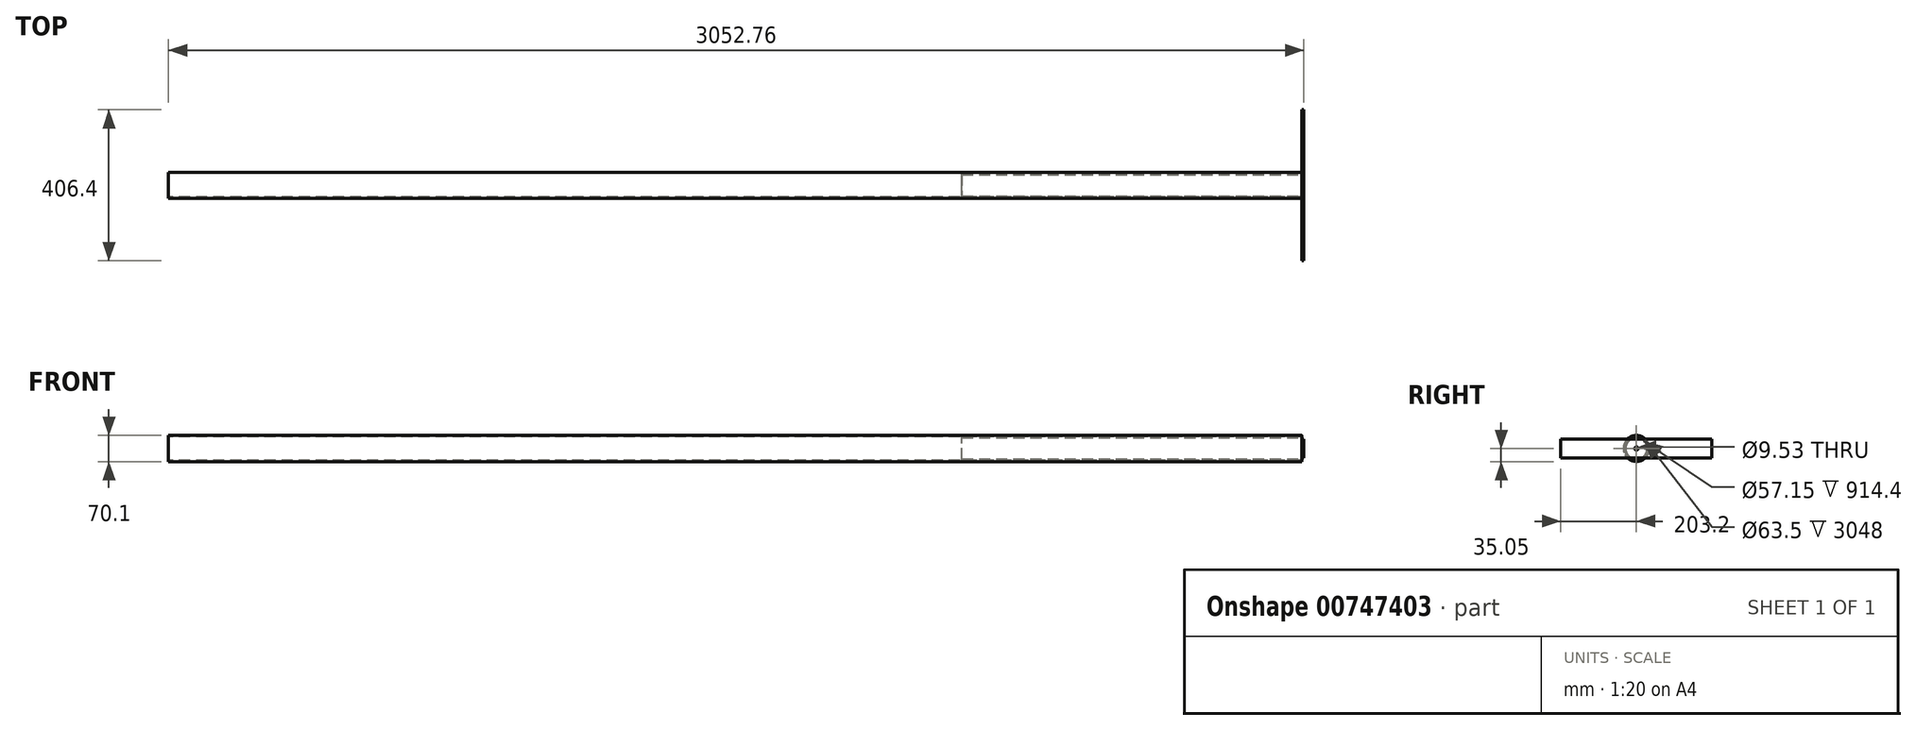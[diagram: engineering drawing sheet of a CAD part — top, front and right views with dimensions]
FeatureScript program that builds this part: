
annotation { "Feature Type Name" : "Feature", "Feature Type Description" : "" }
export const myFeature = defineFeature(function(context is Context, id is Id, definition is map)
    precondition{}
    {
        {
            var Q0;
            Q0=qCreatedBy(makeId("Right.planeOp"),FACE);
            var sketch = newSketch(context, id + "F0", { "sketchPlane" : qUnion([Q0])});
            skCircle(sketch, "E0", {"center": v(0, 0) * mm, "radius": 35.05 * mm});
            skCircle(sketch, "E1", {"center": v(0, 0) * mm, "radius": 31.75 * mm});
            skSolve(sketch);
        }
        {
            var Q0;
            Q0 = qSketchRegion(id + "F0", true);
            extrude(context, id + "F1", {"entities" : qUnion([Q0]), "endBound" : BoundingType.SYMMETRIC, "depth" : 3048 * mm, "offsetDistance" : 25.4 * mm});
        }
        {
            var Q0;
            Q0=makeQuery(id+"F1.opExtrude","CAP_FACE",FACE,{"disambiguationData":[OSD([sQuery(id+"F0.wireOp",EDGE,"E0"),sQuery(id+"F0.wireOp",EDGE,"E1")])],"isStart":false});
            var sketch = newSketch(context, id + "F2", { "sketchPlane" : qUnion([Q0])});
            skCircle(sketch, "E2", {"center": v(0, 0) * mm, "radius": 31.5 * mm});
            skCircle(sketch, "E3", {"center": v(0, 0) * mm, "radius": 28.58 * mm});
            skSolve(sketch);
        }
        {
            var Q0;
            Q0 = qSketchRegion(id + "F2", true);
            extrude(context, id + "F3", {"entities" : qUnion([Q0]), "oppositeDirection" : true, "depth" : 914.4 * mm, "offsetDistance" : 25.4 * mm});
        }
        {
            var Q0;
            Q0=makeQuery(id+"F1.opExtrude","CAP_FACE",FACE,{"disambiguationData":[OSD([sQuery(id+"F0.wireOp",EDGE,"E0"),sQuery(id+"F0.wireOp",EDGE,"E1")])],"isStart":false});
            var sketch = newSketch(context, id + "F4", { "sketchPlane" : qUnion([Q0])});
            skLineSegment(sketch, "E4.bottom", {"start": v(-203.2, -25.4) * mm, "end": v(203.2, -25.4) * mm});
            skLineSegment(sketch, "E4.top", {"start": v(-203.2, 25.4) * mm, "end": v(203.2, 25.4) * mm});
            skLineSegment(sketch, "E4.left", {"start": v(-203.2, -25.4) * mm, "end": v(-203.2, 25.4) * mm});
            skLineSegment(sketch, "E4.right", {"start": v(203.2, -25.4) * mm, "end": v(203.2, 25.4) * mm});
            skPoint(sketch, "E4.middle", {"position": v(0, 0) * mm});
            skSolve(sketch);
        }
        {
            var Q0;
            Q0 = qSketchRegion(id + "F4", true);
            extrude(context, id + "F5", {"entities" : qUnion([Q0]), "depth" : 4.76 * mm, "offsetDistance" : 25.4 * mm});
        }
        {
            var Q0;
            Q0=makeQuery(id+"F5.opExtrude","CAP_FACE",FACE,{"disambiguationData":[OSD([sQuery(id+"F4.wireOp",EDGE,"E4.bottom"),sQuery(id+"F4.wireOp",EDGE,"E4.top"),sQuery(id+"F4.wireOp",EDGE,"E4.left"),sQuery(id+"F4.wireOp",EDGE,"E4.right")])],"isStart":false});
            var sketch = newSketch(context, id + "F6", { "sketchPlane" : qUnion([Q0])});
            skCircle(sketch, "E5", {"center": v(0, 0) * mm, "radius": 4.76 * mm});
            skSolve(sketch);
        }
        {
            var Q0;
            Q0 = qSketchRegion(id + "F6", true);
            extrude(context, id + "F7", {"entities" : qUnion([Q0]), "operationType" : NewBodyOperationType.REMOVE, "endBound" : BoundingType.UP_TO_NEXT, "oppositeDirection" : true, "depth" : 25.4 * mm, "offsetDistance" : 25.4 * mm});
        }
    });
